# Revit family: TakeUp 3 Tier
name_source: partatom
category: Furniture
units: mm (PartAtom-declared; Revit-internal decimal feet)

## family parameters
Always vertical = Yes
Cut with Voids When Loaded = No
OmniClass Number = 23.40.00.00
OmniClass Title = Equipment and Furnishings
Room Calculation Point = No
Shared = No
Work Plane-Based = No

## types (3) — shared parameters
Assembly Code = E2020200
Foot = Gresham - BLACK PLASTIC
Manufacturer = Gresham Office Furniture
Model = TAKE UP
Range = SEATING
Seat (Visibility) = Yes
URL = www.gof.co.uk

## per-type parameters (varying)
| type | Arms | LH Arm | RH Arm | Seat | Tier 1 | Tier 2 | Tier 3 | Top |
| TKULD | Gresham - C | Yes | Yes | <By Category> | Gresham - C | Gresham - C | Gresham - C | Gresham - White MFC |
| TKULL | C | Yes | No | LB | LB | C | C | C |
| TKULR | C | No | Yes | LB | LB | C | C | Gresham - White MFC |

note: column(s) folded — value = type name in every type: Product Code

## geometry (parser evidence)
native form markers: Blend x2, Sweep x1
no freeform markers — native parametric forms only
